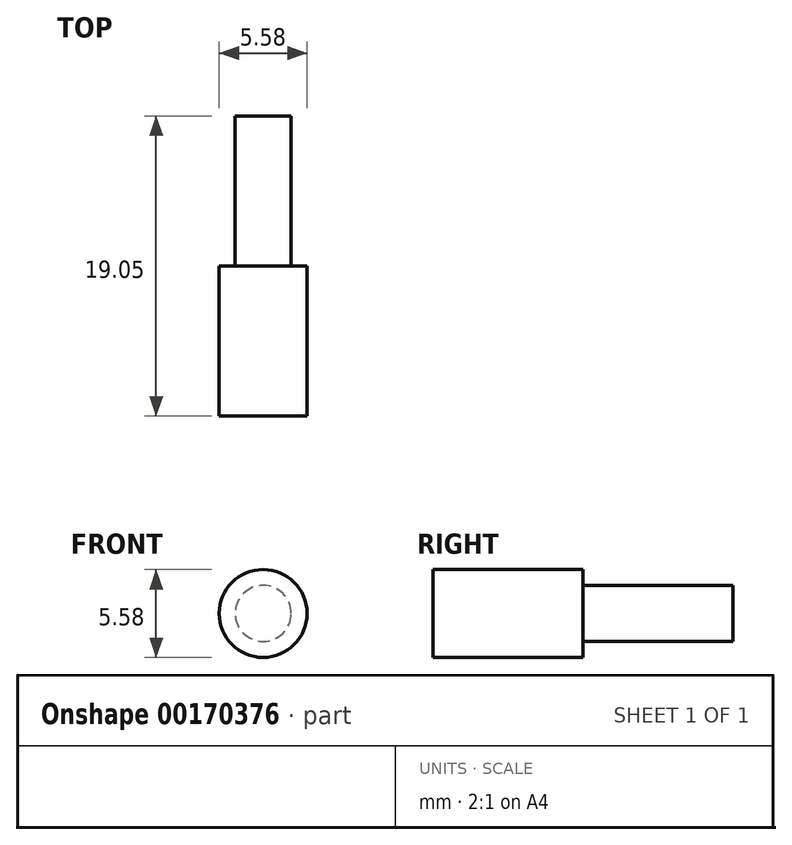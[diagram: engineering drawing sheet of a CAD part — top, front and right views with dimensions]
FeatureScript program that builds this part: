
annotation { "Feature Type Name" : "Feature", "Feature Type Description" : "" }
export const myFeature = defineFeature(function(context is Context, id is Id, definition is map)
    precondition{}
    {
        {
            var Q0;
            Q0=qCreatedBy(makeId("Front.planeOp"),FACE);
            var sketch = newSketch(context, id + "F0", { "sketchPlane" : qUnion([Q0])});
            skCircle(sketch, "E0", {"center": v(0, 0) * mm, "radius": 1.78 * mm});
            skSolve(sketch);
        }
        {
            var Q0;
            Q0=qCreatedBy(makeId("Front.planeOp"),FACE);
            cPlane(context, id + "F1", {"entities" : qUnion([Q0]), "cplaneType" : CPlaneType.OFFSET, "offset" : 19.05 * mm, "width" : 152.4 * mm, "height" : 152.4 * mm});
        }
        {
            var Q0;
            Q0=qCreatedBy(id+"F1.planeOp",FACE);
            var sketch = newSketch(context, id + "F2", { "sketchPlane" : qUnion([Q0])});
            skCircle(sketch, "E1", {"center": v(0, 0) * mm, "radius": 2.8 * mm});
            skSolve(sketch);
        }
        {
            var Q0;
            Q0 = qSketchRegion(id + "F0", true);
            extrude(context, id + "F3", {"entities" : qUnion([Q0]), "depth" : 9.52 * mm});
        }
        {
            var Q0;
            Q0 = qSketchRegion(id + "F2", true);
            extrude(context, id + "F4", {"entities" : qUnion([Q0]), "oppositeDirection" : true, "depth" : 9.52 * mm});
        }
    });
